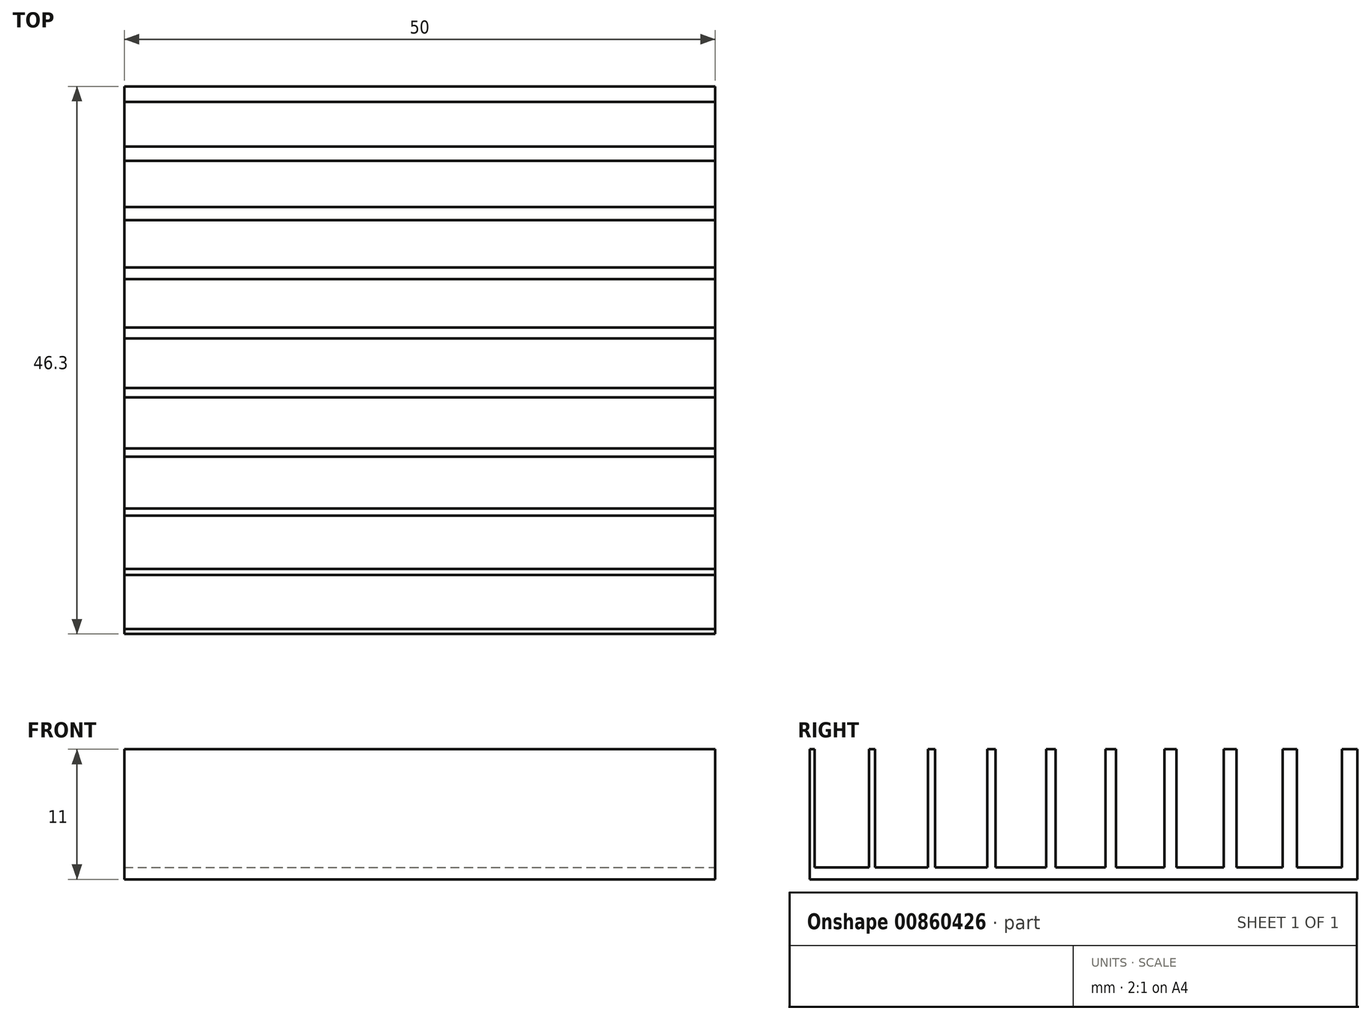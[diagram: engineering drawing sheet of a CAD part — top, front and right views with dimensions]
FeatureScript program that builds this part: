
annotation { "Feature Type Name" : "Feature", "Feature Type Description" : "" }
export const myFeature = defineFeature(function(context is Context, id is Id, definition is map)
    precondition{}
    {
        {
            var Q0;
            Q0=qCreatedBy(makeId("Top.planeOp"),FACE);
            var sketch = newSketch(context, id + "F0", { "sketchPlane" : qUnion([Q0])});
            skLineSegment(sketch, "E0.bottom", {"start": v(25, -23.15) * mm, "end": v(-25, -23.15) * mm});
            skLineSegment(sketch, "E0.top", {"start": v(25, 23.15) * mm, "end": v(-25, 23.15) * mm});
            skLineSegment(sketch, "E0.left", {"start": v(25, -23.15) * mm, "end": v(25, 23.15) * mm});
            skLineSegment(sketch, "E0.right", {"start": v(-25, -23.15) * mm, "end": v(-25, 23.15) * mm});
            skPoint(sketch, "E0.middle", {"position": v(0, 0) * mm});
            skSolve(sketch);
        }
        {
            var Q0;
            Q0 = qSketchRegion(id + "F0", true);
            extrude(context, id + "F1", {"entities" : qUnion([Q0]), "depth" : 1 * mm, "offsetDistance" : 25 * mm});
        }
        {
            var Q0;
            Q0=makeQuery(id+"F1.opExtrude","CAP_FACE",FACE,{"disambiguationData":[OSD([sQuery(id+"F0.wireOp",EDGE,"E0.bottom"),sQuery(id+"F0.wireOp",EDGE,"E0.top"),sQuery(id+"F0.wireOp",EDGE,"E0.left"),sQuery(id+"F0.wireOp",EDGE,"E0.right")])],"isStart":false});
            var sketch = newSketch(context, id + "F2", { "sketchPlane" : qUnion([Q0])});
            skLineSegment(sketch, "E1.bottom", {"start": v(-25, -23.15) * mm, "end": v(25, -23.15) * mm});
            skLineSegment(sketch, "E1.top", {"start": v(-25, -22.75) * mm, "end": v(25, -22.75) * mm});
            skLineSegment(sketch, "E1.left", {"start": v(-25, -23.15) * mm, "end": v(-25, -22.75) * mm});
            skLineSegment(sketch, "E1.right", {"start": v(25, -23.15) * mm, "end": v(25, -22.75) * mm});
            skLineSegment(sketch, "E2.bottom", {"start": v(-25, -18.15) * mm, "end": v(25, -18.15) * mm});
            skLineSegment(sketch, "E2.top", {"start": v(-25, -17.65) * mm, "end": v(25, -17.65) * mm});
            skLineSegment(sketch, "E2.left", {"start": v(-25, -18.15) * mm, "end": v(-25, -17.65) * mm});
            skLineSegment(sketch, "E2.right", {"start": v(25, -18.15) * mm, "end": v(25, -17.65) * mm});
            skLineSegment(sketch, "E3.bottom", {"start": v(-25, -13.15) * mm, "end": v(25, -13.15) * mm});
            skLineSegment(sketch, "E3.top", {"start": v(-25, -12.55) * mm, "end": v(25, -12.55) * mm});
            skLineSegment(sketch, "E3.left", {"start": v(-25, -13.15) * mm, "end": v(-25, -12.55) * mm});
            skLineSegment(sketch, "E3.right", {"start": v(25, -13.15) * mm, "end": v(25, -12.55) * mm});
            skLineSegment(sketch, "E4.bottom", {"start": v(-25, -8.15) * mm, "end": v(25, -8.15) * mm});
            skLineSegment(sketch, "E4.top", {"start": v(-25, -7.45) * mm, "end": v(25, -7.45) * mm});
            skLineSegment(sketch, "E4.left", {"start": v(-25, -8.15) * mm, "end": v(-25, -7.45) * mm});
            skLineSegment(sketch, "E4.right", {"start": v(25, -8.15) * mm, "end": v(25, -7.45) * mm});
            skLineSegment(sketch, "E5.bottom", {"start": v(-25, -3.15) * mm, "end": v(25, -3.15) * mm});
            skLineSegment(sketch, "E5.top", {"start": v(-25, -2.35) * mm, "end": v(25, -2.35) * mm});
            skLineSegment(sketch, "E5.left", {"start": v(-25, -3.15) * mm, "end": v(-25, -2.35) * mm});
            skLineSegment(sketch, "E5.right", {"start": v(25, -3.15) * mm, "end": v(25, -2.35) * mm});
            skLineSegment(sketch, "E6.bottom", {"start": v(-25, 1.85) * mm, "end": v(25, 1.85) * mm});
            skLineSegment(sketch, "E6.top", {"start": v(-25, 2.75) * mm, "end": v(25, 2.75) * mm});
            skLineSegment(sketch, "E6.left", {"start": v(-25, 1.85) * mm, "end": v(-25, 2.75) * mm});
            skLineSegment(sketch, "E6.right", {"start": v(25, 1.85) * mm, "end": v(25, 2.75) * mm});
            skLineSegment(sketch, "E7.bottom", {"start": v(-25, 6.85) * mm, "end": v(25, 6.85) * mm});
            skLineSegment(sketch, "E7.top", {"start": v(-25, 7.85) * mm, "end": v(25, 7.85) * mm});
            skLineSegment(sketch, "E7.left", {"start": v(-25, 6.85) * mm, "end": v(-25, 7.85) * mm});
            skLineSegment(sketch, "E7.right", {"start": v(25, 6.85) * mm, "end": v(25, 7.85) * mm});
            skLineSegment(sketch, "E8.bottom", {"start": v(-25, 11.85) * mm, "end": v(25, 11.85) * mm});
            skLineSegment(sketch, "E8.top", {"start": v(-25, 12.95) * mm, "end": v(25, 12.95) * mm});
            skLineSegment(sketch, "E8.left", {"start": v(-25, 11.85) * mm, "end": v(-25, 12.95) * mm});
            skLineSegment(sketch, "E8.right", {"start": v(25, 11.85) * mm, "end": v(25, 12.95) * mm});
            skLineSegment(sketch, "E9.bottom", {"start": v(-25, 16.85) * mm, "end": v(25, 16.85) * mm});
            skLineSegment(sketch, "E9.top", {"start": v(-25, 18.05) * mm, "end": v(25, 18.05) * mm});
            skLineSegment(sketch, "E9.left", {"start": v(-25, 16.85) * mm, "end": v(-25, 18.05) * mm});
            skLineSegment(sketch, "E9.right", {"start": v(25, 16.85) * mm, "end": v(25, 18.05) * mm});
            skLineSegment(sketch, "E10.bottom", {"start": v(-25, 21.85) * mm, "end": v(25, 21.85) * mm});
            skLineSegment(sketch, "E10.top", {"start": v(-25, 23.15) * mm, "end": v(25, 23.15) * mm});
            skLineSegment(sketch, "E10.left", {"start": v(-25, 21.85) * mm, "end": v(-25, 23.15) * mm});
            skLineSegment(sketch, "E10.right", {"start": v(25, 21.85) * mm, "end": v(25, 23.15) * mm});
            skSolve(sketch);
        }
        {
            var Q0;
            Q0 = qSketchRegion(id + "F2", true);
            extrude(context, id + "F3", {"entities" : qUnion([Q0]), "operationType" : NewBodyOperationType.ADD, "depth" : 10 * mm, "offsetDistance" : 25 * mm});
        }
    });
